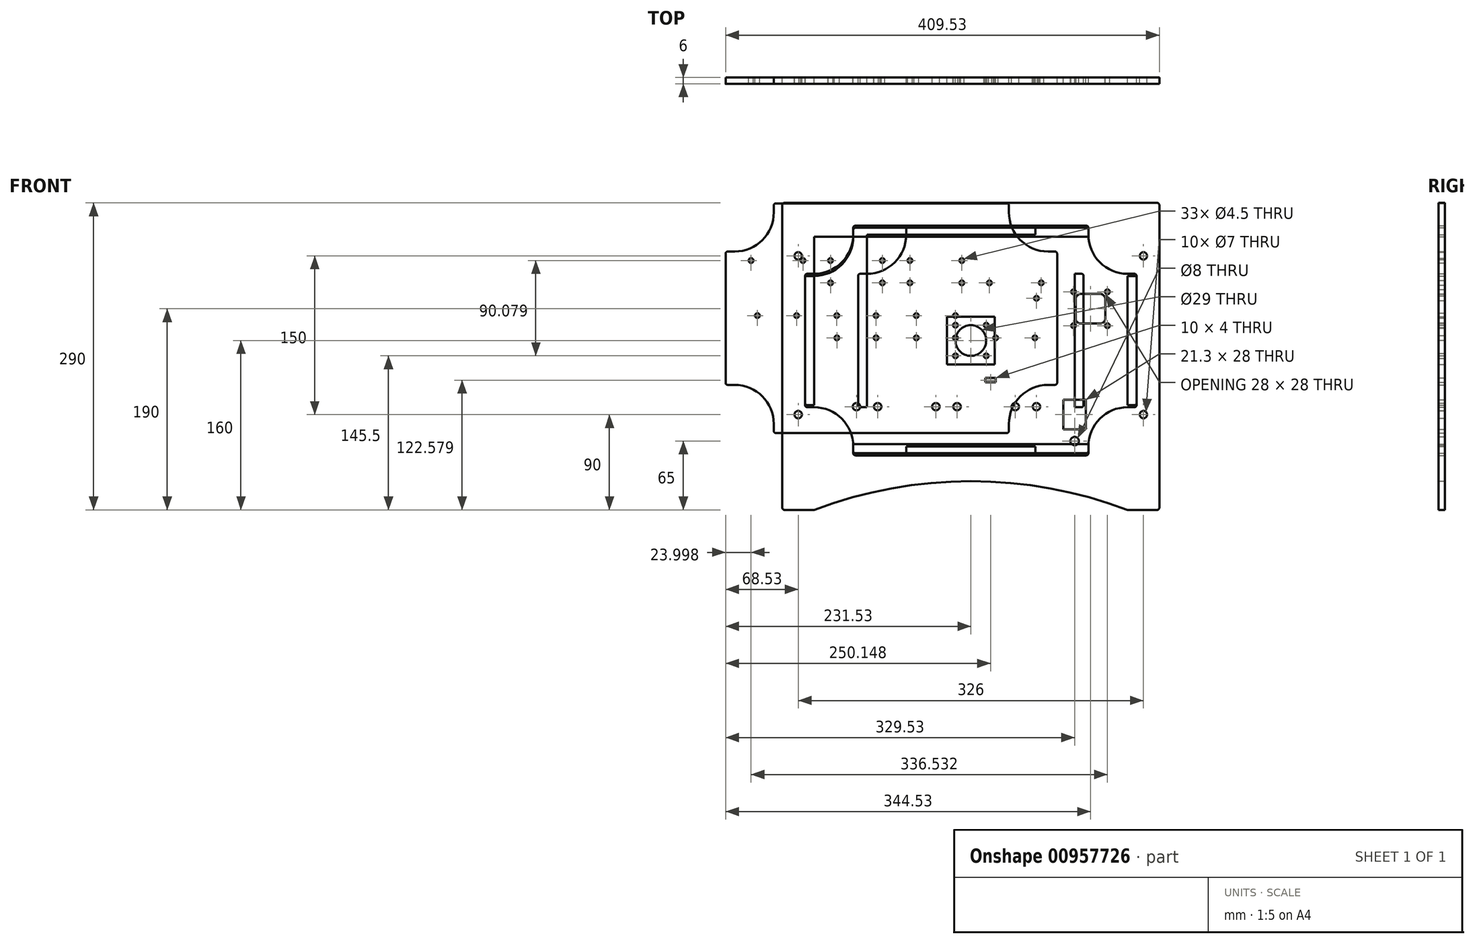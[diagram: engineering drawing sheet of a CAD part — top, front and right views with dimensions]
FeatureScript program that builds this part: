
annotation { "Feature Type Name" : "Feature", "Feature Type Description" : "" }
export const myFeature = defineFeature(function(context is Context, id is Id, definition is map)
    precondition{}
    {
        {
            var Q0;
            Q0=qCreatedBy(makeId("Front.planeOp"),FACE);
            var sketch = newSketch(context, id + "F0", { "sketchPlane" : qUnion([Q0])});
            skLineSegment(sketch, "E0.bottom", {"start": v(-148, 100) * mm, "end": v(148, 100) * mm});
            skLineSegment(sketch, "E0.top", {"start": v(-148, -100) * mm, "end": v(148, -100) * mm});
            skLineSegment(sketch, "E0.left", {"start": v(-148, 100) * mm, "end": v(-148, -100) * mm});
            skLineSegment(sketch, "E0.right", {"start": v(148, 100) * mm, "end": v(148, -100) * mm});
            skPoint(sketch, "E0.middle", {"position": v(0, 0) * mm});
            skPoint(sketch, "E1", {"position": v(-108, 30) * mm});
            skPoint(sketch, "E2", {"position": v(-33, 30) * mm});
            skPoint(sketch, "E3", {"position": v(42, 30) * mm});
            skLineSegment(sketch, "E4.bottom", {"start": v(-75.5, 62.5) * mm, "end": v(-140.5, 62.5) * mm});
            skLineSegment(sketch, "E4.top", {"start": v(-75.5, -2.5) * mm, "end": v(-140.5, -2.5) * mm});
            skLineSegment(sketch, "E4.left", {"start": v(-75.5, 62.5) * mm, "end": v(-75.5, -2.5) * mm});
            skLineSegment(sketch, "E4.right", {"start": v(-140.5, 62.5) * mm, "end": v(-140.5, -2.5) * mm});
            skLineSegment(sketch, "E5.bottom", {"start": v(-0.5, 62.5) * mm, "end": v(-65.5, 62.5) * mm});
            skLineSegment(sketch, "E5.top", {"start": v(-0.5, -2.5) * mm, "end": v(-65.5, -2.5) * mm});
            skLineSegment(sketch, "E5.left", {"start": v(-0.5, 62.5) * mm, "end": v(-0.5, -2.5) * mm});
            skLineSegment(sketch, "E5.right", {"start": v(-65.5, 62.5) * mm, "end": v(-65.5, -2.5) * mm});
            skLineSegment(sketch, "E6.bottom", {"start": v(74.5, 62.5) * mm, "end": v(9.5, 62.5) * mm});
            skLineSegment(sketch, "E6.top", {"start": v(74.5, -2.5) * mm, "end": v(9.5, -2.5) * mm});
            skLineSegment(sketch, "E6.left", {"start": v(74.5, 62.5) * mm, "end": v(74.5, -2.5) * mm});
            skLineSegment(sketch, "E6.right", {"start": v(9.5, 62.5) * mm, "end": v(9.5, -2.5) * mm});
            skPoint(sketch, "E7", {"position": v(-132.5, 54.5) * mm});
            skCircle(sketch, "E8", {"center": v(-132.5, 54.5) * mm, "radius": 2.25 * mm});
            skPoint(sketch, "E9", {"position": v(-57.5, 54.5) * mm});
            skPoint(sketch, "E10", {"position": v(17.5, 54.5) * mm});
            skCircle(sketch, "E11", {"center": v(-57.5, 54.5) * mm, "radius": 2.25 * mm});
            skCircle(sketch, "E12", {"center": v(17.5, 54.5) * mm, "radius": 2.25 * mm});
            skLineSegment(sketch, "E13", {"start": v(-33, 62.5) * mm, "end": v(-33, -2.5) * mm});
            skLineSegment(sketch, "E14", {"start": v(42, 62.5) * mm, "end": v(42, -2.5) * mm});
            skLineSegment(sketch, "E15", {"start": v(-108, 62.5) * mm, "end": v(-108, -2.5) * mm});
            skPoint(sketch, "E16", {"position": v(-126.5, 2.5) * mm});
            skPoint(sketch, "E17", {"position": v(-51.5, 2.5) * mm});
            skPoint(sketch, "E18", {"position": v(23.5, 2.5) * mm});
            skCircle(sketch, "E19", {"center": v(23.5, 2.5) * mm, "radius": 2.25 * mm});
            skCircle(sketch, "E20", {"center": v(-51.5, 2.5) * mm, "radius": 2.25 * mm});
            skCircle(sketch, "E21", {"center": v(-126.5, 2.5) * mm, "radius": 2.25 * mm});
            skArc(sketch, "E22", {"start": v(-111, 100) * mm, "mid": v(-121.84, 73.84) * mm, "end": v(-148, 63) * mm});
            skArc(sketch, "E23", {"start": v(111, 100) * mm, "mid": v(121.84, 73.84) * mm, "end": v(148, 63) * mm});
            skArc(sketch, "E24", {"start": v(148, -63) * mm, "mid": v(121.84, -73.84) * mm, "end": v(111, -100) * mm});
            skArc(sketch, "E25", {"start": v(-148, -63) * mm, "mid": v(-121.84, -73.84) * mm, "end": v(-111, -100) * mm});
            skPoint(sketch, "E26", {"position": v(-108, -62.5) * mm});
            skPoint(sketch, "E27", {"position": v(-88, -62.5) * mm});
            skPoint(sketch, "E28", {"position": v(-33, -62.5) * mm});
            skPoint(sketch, "E29", {"position": v(-13, -62.5) * mm});
            skPoint(sketch, "E30", {"position": v(42, -62.5) * mm});
            skPoint(sketch, "E31", {"position": v(62, -62.5) * mm});
            skCircle(sketch, "E32", {"center": v(-108, -62.5) * mm, "radius": 3.5 * mm});
            skCircle(sketch, "E33", {"center": v(-88, -62.5) * mm, "radius": 3.5 * mm});
            skCircle(sketch, "E34", {"center": v(-33, -62.5) * mm, "radius": 3.5 * mm});
            skCircle(sketch, "E35", {"center": v(-13, -62.5) * mm, "radius": 3.5 * mm});
            skCircle(sketch, "E36", {"center": v(42, -62.5) * mm, "radius": 3.5 * mm});
            skCircle(sketch, "E37", {"center": v(62, -62.5) * mm, "radius": 3.5 * mm});
            skPoint(sketch, "E38", {"position": v(98, -70) * mm});
            skLineSegment(sketch, "E39.bottom", {"start": v(87.35, -56) * mm, "end": v(108.65, -56) * mm});
            skLineSegment(sketch, "E39.top", {"start": v(87.35, -84) * mm, "end": v(108.65, -84) * mm});
            skLineSegment(sketch, "E39.left", {"start": v(87.35, -56) * mm, "end": v(87.35, -84) * mm});
            skLineSegment(sketch, "E39.right", {"start": v(108.65, -56) * mm, "end": v(108.65, -84) * mm});
            skPoint(sketch, "E40", {"position": v(113, 30) * mm});
            skLineSegment(sketch, "E41.bottom", {"start": v(132.75, 49.75) * mm, "end": v(93.25, 49.75) * mm});
            skLineSegment(sketch, "E41.top", {"start": v(132.75, 10.25) * mm, "end": v(93.25, 10.25) * mm});
            skLineSegment(sketch, "E41.left", {"start": v(132.75, 49.75) * mm, "end": v(132.75, 10.25) * mm});
            skLineSegment(sketch, "E41.right", {"start": v(93.25, 49.75) * mm, "end": v(93.25, 10.25) * mm});
            skPoint(sketch, "E42", {"position": v(97, 46) * mm});
            skCircle(sketch, "E43", {"center": v(97, 46) * mm, "radius": 2.25 * mm});
            skPoint(sketch, "E44.0.1.0", {"position": v(97, 14) * mm});
            skCircle(sketch, "E44.0.1.1", {"center": v(97, 14) * mm, "radius": 2.25 * mm});
            skPoint(sketch, "E44.1.0.0", {"position": v(129, 46) * mm});
            skCircle(sketch, "E44.1.0.1", {"center": v(129, 46) * mm, "radius": 2.25 * mm});
            skPoint(sketch, "E44.1.1.0", {"position": v(129, 14) * mm});
            skCircle(sketch, "E44.1.1.1", {"center": v(129, 14) * mm, "radius": 2.25 * mm});
            skLineSegment(sketch, "E44.direction1", {"start": v(97, 46) * mm, "end": v(129, 46) * mm, "construction": true});
            skLineSegment(sketch, "E44.direction2", {"start": v(97, 46) * mm, "end": v(97, 14) * mm, "construction": true});
            skCircle(sketch, "E45.MirrorC", {"center": v(-83.5, 54.5) * mm, "radius": 2.25 * mm});
            skCircle(sketch, "E46.MirrorC", {"center": v(-89.5, 2.5) * mm, "radius": 2.25 * mm});
            skCircle(sketch, "E47.MirrorC", {"center": v(-8.5, 54.5) * mm, "radius": 2.25 * mm});
            skCircle(sketch, "E48.MirrorC", {"center": v(-14.5, 2.5) * mm, "radius": 2.25 * mm});
            skCircle(sketch, "E49.MirrorC", {"center": v(66.5, 54.5) * mm, "radius": 2.25 * mm});
            skCircle(sketch, "E50.MirrorC", {"center": v(60.5, 2.5) * mm, "radius": 2.25 * mm});
            skLineSegment(sketch, "E51.bottom", {"start": v(122, 16) * mm, "end": v(104, 16) * mm});
            skLineSegment(sketch, "E51.top", {"start": v(122, 44) * mm, "end": v(104, 44) * mm});
            skLineSegment(sketch, "E51.left", {"start": v(127, 21) * mm, "end": v(127, 39) * mm});
            skLineSegment(sketch, "E51.right", {"start": v(99, 21) * mm, "end": v(99, 39) * mm});
            skPoint(sketch, "E52.visualSharp", {"position": v(99, 44) * mm});
            skArc(sketch, "E52.filletArc", {"start": v(104, 44) * mm, "mid": v(100.46, 42.54) * mm, "end": v(99, 39) * mm});
            skPoint(sketch, "E53.visualSharp", {"position": v(127, 44) * mm});
            skArc(sketch, "E53.filletArc", {"start": v(127, 39) * mm, "mid": v(125.54, 42.54) * mm, "end": v(122, 44) * mm});
            skPoint(sketch, "E54.visualSharp", {"position": v(127, 16) * mm});
            skArc(sketch, "E54.filletArc", {"start": v(122, 16) * mm, "mid": v(125.54, 17.46) * mm, "end": v(127, 21) * mm});
            skPoint(sketch, "E55.visualSharp", {"position": v(99, 16) * mm});
            skArc(sketch, "E55.filletArc", {"start": v(99, 21) * mm, "mid": v(100.46, 17.46) * mm, "end": v(104, 16) * mm});
            skLineSegment(sketch, "E56.bottom", {"start": v(-111, 100) * mm, "end": v(111, 100) * mm});
            skLineSegment(sketch, "E56.top", {"start": v(-109, 108.5) * mm, "end": v(109, 108.5) * mm});
            skLineSegment(sketch, "E56.left", {"start": v(-111, 100) * mm, "end": v(-111, 106.5) * mm});
            skLineSegment(sketch, "E56.right", {"start": v(111, 100) * mm, "end": v(111, 106.5) * mm});
            skLineSegment(sketch, "E57.bottom", {"start": v(-111, -100) * mm, "end": v(111, -100) * mm});
            skLineSegment(sketch, "E57.top", {"start": v(-109, -108.5) * mm, "end": v(109, -108.5) * mm});
            skLineSegment(sketch, "E57.left", {"start": v(-111, -100) * mm, "end": v(-111, -106.5) * mm});
            skLineSegment(sketch, "E57.right", {"start": v(111, -100) * mm, "end": v(111, -106.5) * mm});
            skLineSegment(sketch, "E58.bottom", {"start": v(-148, 63) * mm, "end": v(-154.5, 63) * mm});
            skLineSegment(sketch, "E58.top", {"start": v(-148, -63) * mm, "end": v(-154.5, -63) * mm});
            skLineSegment(sketch, "E58.left", {"start": v(-148, 63) * mm, "end": v(-148, -63) * mm});
            skLineSegment(sketch, "E58.right", {"start": v(-156.5, 61) * mm, "end": v(-156.5, -61) * mm});
            skLineSegment(sketch, "E59.bottom", {"start": v(148, 63) * mm, "end": v(154.5, 63) * mm});
            skLineSegment(sketch, "E59.top", {"start": v(148, -63) * mm, "end": v(154.5, -63) * mm});
            skLineSegment(sketch, "E59.left", {"start": v(148, 63) * mm, "end": v(148, -63) * mm});
            skLineSegment(sketch, "E59.right", {"start": v(156.5, 61) * mm, "end": v(156.5, -61) * mm});
            skPoint(sketch, "E60.visualSharp", {"position": v(-111, 108.5) * mm});
            skArc(sketch, "E60.filletArc", {"start": v(-109, 108.5) * mm, "mid": v(-110.41, 107.91) * mm, "end": v(-111, 106.5) * mm});
            skPoint(sketch, "E61.visualSharp", {"position": v(111, 108.5) * mm});
            skArc(sketch, "E61.filletArc", {"start": v(111, 106.5) * mm, "mid": v(110.41, 107.91) * mm, "end": v(109, 108.5) * mm});
            skPoint(sketch, "E62.visualSharp", {"position": v(156.5, 63) * mm});
            skArc(sketch, "E62.filletArc", {"start": v(156.5, 61) * mm, "mid": v(155.91, 62.41) * mm, "end": v(154.5, 63) * mm});
            skPoint(sketch, "E63.visualSharp", {"position": v(156.5, -63) * mm});
            skArc(sketch, "E63.filletArc", {"start": v(154.5, -63) * mm, "mid": v(155.91, -62.41) * mm, "end": v(156.5, -61) * mm});
            skPoint(sketch, "E64.visualSharp", {"position": v(111, -108.5) * mm});
            skArc(sketch, "E64.filletArc", {"start": v(109, -108.5) * mm, "mid": v(110.41, -107.91) * mm, "end": v(111, -106.5) * mm});
            skPoint(sketch, "E65.visualSharp", {"position": v(-111, -108.5) * mm});
            skArc(sketch, "E65.filletArc", {"start": v(-111, -106.5) * mm, "mid": v(-110.41, -107.91) * mm, "end": v(-109, -108.5) * mm});
            skPoint(sketch, "E66.visualSharp", {"position": v(-156.5, -63) * mm});
            skArc(sketch, "E66.filletArc", {"start": v(-156.5, -61) * mm, "mid": v(-155.91, -62.41) * mm, "end": v(-154.5, -63) * mm});
            skPoint(sketch, "E67.visualSharp", {"position": v(-156.5, 63) * mm});
            skArc(sketch, "E67.filletArc", {"start": v(-154.5, 63) * mm, "mid": v(-155.91, 62.41) * mm, "end": v(-156.5, 61) * mm});
            skPoint(sketch, "E68", {"position": v(98, -95) * mm});
            skPoint(sketch, "E68.positionSnap0", {"position": v(98, -84) * mm});
            skCircle(sketch, "E69", {"center": v(98, -95) * mm, "radius": 4 * mm});
            skSolve(sketch);
        }
        {
            var Q0;
            {var subQ28=sQuery(id+"F0.wireOp",EDGE,"E4.left");Q0=makeQuery(id+"F0.imprint","IMPRINT",FACE,{"disambiguationData":[TD([[makeQuery(id+"F0.imprint","IMPRINT",EDGE,{"derivedFrom":subQ28}),1.0]])]});}
            var Q1;
            {var subQ0=sQuery(id+"F0.wireOp",EDGE,"E4.left");Q1=makeQuery(id+"F0.imprint","IMPRINT",FACE,{"disambiguationData":[TD([[makeQuery(id+"F0.imprint","IMPRINT",EDGE,{"derivedFrom":subQ0}),-1.0]])]});}
            var Q2;
            {var subQ0=sQuery(id+"F0.wireOp",EDGE,"E5.right");Q2=makeQuery(id+"F0.imprint","IMPRINT",FACE,{"disambiguationData":[TD([[makeQuery(id+"F0.imprint","IMPRINT",EDGE,{"derivedFrom":subQ0}),1.0]])]});}
            var Q3;
            {var subQ1=sQuery(id+"F0.wireOp",EDGE,"E5.left");Q3=makeQuery(id+"F0.imprint","IMPRINT",FACE,{"disambiguationData":[TD([[makeQuery(id+"F0.imprint","IMPRINT",EDGE,{"derivedFrom":subQ1}),-1.0]])]});}
            var Q4;
            {var subQ2=sQuery(id+"F0.wireOp",EDGE,"E4.right");Q4=makeQuery(id+"F0.imprint","IMPRINT",FACE,{"disambiguationData":[TD([[makeQuery(id+"F0.imprint","IMPRINT",EDGE,{"derivedFrom":subQ2}),1.0]])]});}
            var Q5;
            {var subQ0=sQuery(id+"F0.wireOp",EDGE,"E6.right");Q5=makeQuery(id+"F0.imprint","IMPRINT",FACE,{"disambiguationData":[TD([[makeQuery(id+"F0.imprint","IMPRINT",EDGE,{"derivedFrom":subQ0}),1.0]])]});}
            var Q6;
            {var subQ0=sQuery(id+"F0.wireOp",EDGE,"E6.left");Q6=makeQuery(id+"F0.imprint","IMPRINT",FACE,{"disambiguationData":[TD([[makeQuery(id+"F0.imprint","IMPRINT",EDGE,{"derivedFrom":subQ0}),-1.0]])]});}
            var Q7;
            Q7=makeQuery(id+"F0.imprint","IMPRINT",FACE,{"disambiguationData":[TD([[makeQuery(id+"F0.imprint","IMPRINT",EDGE,{"derivedFrom":sQuery(id+"F0.wireOp",EDGE,"E41.bottom")}),1.0]])]});
            var Q8;
            {var subQ0=sQuery(id+"F0.wireOp",EDGE,"E58.bottom");Q8=makeQuery(id+"F0.imprint","IMPRINT",FACE,{"disambiguationData":[TD([[makeQuery(id+"F0.imprint","IMPRINT",EDGE,{"derivedFrom":subQ0}),1.0]])]});}
            var Q9;
            Q9=makeQuery(id+"F0.imprint","IMPRINT",FACE,{"disambiguationData":[TD([[makeQuery(id+"F0.imprint","IMPRINT",EDGE,{"derivedFrom":sQuery(id+"F0.wireOp",EDGE,"E56.top")}),-1.0]])]});
            var Q10;
            {var subQ0=sQuery(id+"F0.wireOp",EDGE,"E59.bottom");Q10=makeQuery(id+"F0.imprint","IMPRINT",FACE,{"disambiguationData":[TD([[makeQuery(id+"F0.imprint","IMPRINT",EDGE,{"derivedFrom":subQ0}),-1.0]])]});}
            var Q11;
            Q11=makeQuery(id+"F0.imprint","IMPRINT",FACE,{"disambiguationData":[TD([[makeQuery(id+"F0.imprint","IMPRINT",EDGE,{"derivedFrom":sQuery(id+"F0.wireOp",EDGE,"E57.top")}),1.0]])]});
            extrude(context, id + "F1", {"entities" : qUnion([Q0, Q1, Q2, Q3, Q4, Q5, Q6, Q7, Q8, Q9, Q10, Q11]), "depth" : 6 * mm, "offsetDistance" : 25 * mm});
        }
        {
            var Q0;
            Q0=qCreatedBy(makeId("Front.planeOp"),FACE);
            var sketch = newSketch(context, id + "F2", { "sketchPlane" : qUnion([Q0])});
            skLineSegment(sketch, "E70.bottom", {"start": v(-223.03, 121.08) * mm, "end": v(72.97, 121.08) * mm});
            skLineSegment(sketch, "E70.top", {"start": v(-223.03, -78.92) * mm, "end": v(72.97, -78.92) * mm});
            skLineSegment(sketch, "E70.left", {"start": v(-223.03, 121.08) * mm, "end": v(-223.03, -78.92) * mm});
            skLineSegment(sketch, "E70.right", {"start": v(72.97, 121.08) * mm, "end": v(72.97, -78.92) * mm});
            skPoint(sketch, "E70.middle", {"position": v(-75.03, 21.08) * mm});
            skPoint(sketch, "E71", {"position": v(-183.03, 51.08) * mm});
            skPoint(sketch, "E72", {"position": v(-108.03, 51.08) * mm});
            skPoint(sketch, "E73", {"position": v(-33.03, 51.08) * mm});
            skLineSegment(sketch, "E74.bottom", {"start": v(-150.53, 83.58) * mm, "end": v(-215.53, 83.58) * mm});
            skLineSegment(sketch, "E74.top", {"start": v(-150.53, 18.58) * mm, "end": v(-215.53, 18.58) * mm});
            skLineSegment(sketch, "E74.left", {"start": v(-150.53, 83.58) * mm, "end": v(-150.53, 18.58) * mm});
            skLineSegment(sketch, "E74.right", {"start": v(-215.53, 83.58) * mm, "end": v(-215.53, 18.58) * mm});
            skLineSegment(sketch, "E75.bottom", {"start": v(-75.53, 83.58) * mm, "end": v(-140.53, 83.58) * mm});
            skLineSegment(sketch, "E75.top", {"start": v(-75.53, 18.58) * mm, "end": v(-140.53, 18.58) * mm});
            skLineSegment(sketch, "E75.left", {"start": v(-75.53, 83.58) * mm, "end": v(-75.53, 18.58) * mm});
            skLineSegment(sketch, "E75.right", {"start": v(-140.53, 83.58) * mm, "end": v(-140.53, 18.58) * mm});
            skLineSegment(sketch, "E76.bottom", {"start": v(-0.53, 83.58) * mm, "end": v(-65.53, 83.58) * mm});
            skLineSegment(sketch, "E76.top", {"start": v(-0.53, 18.58) * mm, "end": v(-65.53, 18.58) * mm});
            skLineSegment(sketch, "E76.left", {"start": v(-0.53, 83.58) * mm, "end": v(-0.53, 18.58) * mm});
            skLineSegment(sketch, "E76.right", {"start": v(-65.53, 83.58) * mm, "end": v(-65.53, 18.58) * mm});
            skPoint(sketch, "E77", {"position": v(-207.53, 75.58) * mm});
            skCircle(sketch, "E78", {"center": v(-207.53, 75.58) * mm, "radius": 2.25 * mm});
            skPoint(sketch, "E79", {"position": v(-132.53, 75.58) * mm});
            skPoint(sketch, "E80", {"position": v(-57.53, 75.58) * mm});
            skCircle(sketch, "E81", {"center": v(-132.53, 75.58) * mm, "radius": 2.25 * mm});
            skCircle(sketch, "E82", {"center": v(-57.53, 75.58) * mm, "radius": 2.25 * mm});
            skLineSegment(sketch, "E83", {"start": v(-108.03, 83.58) * mm, "end": v(-108.03, 18.58) * mm});
            skLineSegment(sketch, "E84", {"start": v(-33.03, 83.58) * mm, "end": v(-33.03, 18.58) * mm});
            skLineSegment(sketch, "E85", {"start": v(-183.03, 83.58) * mm, "end": v(-183.03, 18.58) * mm});
            skPoint(sketch, "E86", {"position": v(-201.53, 23.58) * mm});
            skPoint(sketch, "E87", {"position": v(-126.53, 23.58) * mm});
            skPoint(sketch, "E88", {"position": v(-51.53, 23.58) * mm});
            skCircle(sketch, "E89", {"center": v(-51.53, 23.58) * mm, "radius": 2.25 * mm});
            skCircle(sketch, "E90", {"center": v(-126.53, 23.58) * mm, "radius": 2.25 * mm});
            skCircle(sketch, "E91", {"center": v(-201.53, 23.58) * mm, "radius": 2.25 * mm});
            skArc(sketch, "E92", {"start": v(-186.03, 121.08) * mm, "mid": v(-196.87, 94.92) * mm, "end": v(-223.03, 84.08) * mm});
            skArc(sketch, "E93", {"start": v(35.97, 121.08) * mm, "mid": v(46.8, 94.92) * mm, "end": v(72.97, 84.08) * mm});
            skArc(sketch, "E94", {"start": v(72.97, -41.92) * mm, "mid": v(46.8, -52.76) * mm, "end": v(35.97, -78.92) * mm});
            skArc(sketch, "E95", {"start": v(-223.03, -41.92) * mm, "mid": v(-196.87, -52.76) * mm, "end": v(-186.03, -78.92) * mm});
            skCircle(sketch, "E96.MirrorC", {"center": v(-158.53, 75.58) * mm, "radius": 2.25 * mm});
            skCircle(sketch, "E97.MirrorC", {"center": v(-164.53, 23.58) * mm, "radius": 2.25 * mm});
            skCircle(sketch, "E98.MirrorC", {"center": v(-83.53, 75.58) * mm, "radius": 2.25 * mm});
            skCircle(sketch, "E99.MirrorC", {"center": v(-89.53, 23.58) * mm, "radius": 2.25 * mm});
            skCircle(sketch, "E100.MirrorC", {"center": v(-8.53, 75.58) * mm, "radius": 2.25 * mm});
            skCircle(sketch, "E101.MirrorC", {"center": v(-14.53, 23.58) * mm, "radius": 2.25 * mm});
            skLineSegment(sketch, "E102.bottom", {"start": v(-186.03, 121.08) * mm, "end": v(35.97, 121.08) * mm});
            skLineSegment(sketch, "E102.top", {"start": v(-184.03, 129.58) * mm, "end": v(33.97, 129.58) * mm});
            skLineSegment(sketch, "E102.left", {"start": v(-186.03, 121.08) * mm, "end": v(-186.03, 127.58) * mm});
            skLineSegment(sketch, "E102.right", {"start": v(35.97, 121.08) * mm, "end": v(35.97, 127.58) * mm});
            skLineSegment(sketch, "E103.bottom", {"start": v(-186.03, -78.92) * mm, "end": v(35.97, -78.92) * mm});
            skLineSegment(sketch, "E103.top", {"start": v(-184.03, -87.42) * mm, "end": v(33.97, -87.42) * mm});
            skLineSegment(sketch, "E103.left", {"start": v(-186.03, -78.92) * mm, "end": v(-186.03, -85.42) * mm});
            skLineSegment(sketch, "E103.right", {"start": v(35.97, -78.92) * mm, "end": v(35.97, -85.42) * mm});
            skLineSegment(sketch, "E104.bottom", {"start": v(-223.03, 84.08) * mm, "end": v(-229.53, 84.08) * mm});
            skLineSegment(sketch, "E104.top", {"start": v(-223.03, -41.92) * mm, "end": v(-229.53, -41.92) * mm});
            skLineSegment(sketch, "E104.left", {"start": v(-223.03, 84.08) * mm, "end": v(-223.03, -41.92) * mm});
            skLineSegment(sketch, "E104.right", {"start": v(-231.53, 82.08) * mm, "end": v(-231.53, -39.92) * mm});
            skLineSegment(sketch, "E105.bottom", {"start": v(72.97, 84.08) * mm, "end": v(79.47, 84.08) * mm});
            skLineSegment(sketch, "E105.top", {"start": v(72.97, -41.92) * mm, "end": v(79.47, -41.92) * mm});
            skLineSegment(sketch, "E105.left", {"start": v(72.97, 84.08) * mm, "end": v(72.97, -41.92) * mm});
            skLineSegment(sketch, "E105.right", {"start": v(81.47, 82.08) * mm, "end": v(81.47, -39.92) * mm});
            skPoint(sketch, "E106", {"position": v(37.97, 1.08) * mm});
            skLineSegment(sketch, "E107.bottom", {"start": v(66.97, 43.58) * mm, "end": v(8.97, 43.58) * mm});
            skLineSegment(sketch, "E107.top", {"start": v(66.97, -41.42) * mm, "end": v(8.97, -41.42) * mm});
            skLineSegment(sketch, "E107.left", {"start": v(66.97, 43.58) * mm, "end": v(66.97, -41.42) * mm});
            skLineSegment(sketch, "E107.right", {"start": v(8.97, 43.58) * mm, "end": v(8.97, -41.42) * mm});
            skPoint(sketch, "E108", {"position": v(62.02, 39.93) * mm});
            skCircle(sketch, "E109", {"center": v(62.02, 39.93) * mm, "radius": 2.25 * mm});
            skPoint(sketch, "E110", {"position": v(13.62, -41.42) * mm});
            skLineSegment(sketch, "E111", {"start": v(13.62, -41.42) * mm, "end": v(13.62, -39.42) * mm});
            skLineSegment(sketch, "E112.bottom", {"start": v(13.62, -39.42) * mm, "end": v(23.62, -39.42) * mm});
            skLineSegment(sketch, "E112.top", {"start": v(13.62, -35.42) * mm, "end": v(23.62, -35.42) * mm});
            skLineSegment(sketch, "E112.left", {"start": v(13.62, -39.42) * mm, "end": v(13.62, -35.42) * mm});
            skLineSegment(sketch, "E112.right", {"start": v(23.62, -39.42) * mm, "end": v(23.62, -35.42) * mm});
            skPoint(sketch, "E113.visualSharp", {"position": v(-186.03, 129.58) * mm});
            skArc(sketch, "E113.filletArc", {"start": v(-184.03, 129.58) * mm, "mid": v(-185.45, 129) * mm, "end": v(-186.03, 127.58) * mm});
            skPoint(sketch, "E114.visualSharp", {"position": v(35.97, 129.58) * mm});
            skArc(sketch, "E114.filletArc", {"start": v(35.97, 127.58) * mm, "mid": v(35.38, 129) * mm, "end": v(33.97, 129.58) * mm});
            skPoint(sketch, "E115.visualSharp", {"position": v(81.47, 84.08) * mm});
            skArc(sketch, "E115.filletArc", {"start": v(81.47, 82.08) * mm, "mid": v(80.88, 83.5) * mm, "end": v(79.47, 84.08) * mm});
            skPoint(sketch, "E116.visualSharp", {"position": v(81.47, -41.92) * mm});
            skArc(sketch, "E116.filletArc", {"start": v(79.47, -41.92) * mm, "mid": v(80.88, -41.34) * mm, "end": v(81.47, -39.92) * mm});
            skPoint(sketch, "E117.visualSharp", {"position": v(35.97, -87.42) * mm});
            skArc(sketch, "E117.filletArc", {"start": v(33.97, -87.42) * mm, "mid": v(35.38, -86.84) * mm, "end": v(35.97, -85.42) * mm});
            skPoint(sketch, "E118.visualSharp", {"position": v(-186.03, -87.42) * mm});
            skArc(sketch, "E118.filletArc", {"start": v(-186.03, -85.42) * mm, "mid": v(-185.45, -86.84) * mm, "end": v(-184.03, -87.42) * mm});
            skPoint(sketch, "E119.visualSharp", {"position": v(-231.53, -41.92) * mm});
            skArc(sketch, "E119.filletArc", {"start": v(-231.53, -39.92) * mm, "mid": v(-230.95, -41.34) * mm, "end": v(-229.53, -41.92) * mm});
            skPoint(sketch, "E120.visualSharp", {"position": v(-231.53, 84.08) * mm});
            skArc(sketch, "E120.filletArc", {"start": v(-229.53, 84.08) * mm, "mid": v(-230.95, 83.5) * mm, "end": v(-231.53, 82.08) * mm});
            skSolve(sketch);
        }
        {
            var Q0;
            {var subQ24=sQuery(id+"F2.wireOp",EDGE,"E74.left");Q0=makeQuery(id+"F2.imprint","IMPRINT",FACE,{"disambiguationData":[TD([[makeQuery(id+"F2.imprint","IMPRINT",EDGE,{"derivedFrom":subQ24}),1.0]])]});}
            var Q1;
            Q1=makeQuery(id+"F2.imprint","IMPRINT",FACE,{"disambiguationData":[TD([[makeQuery(id+"F2.imprint","IMPRINT",EDGE,{"derivedFrom":sQuery(id+"F2.wireOp",EDGE,"E102.top")}),-1.0]])]});
            var Q2;
            {var subQ0=sQuery(id+"F2.wireOp",EDGE,"E105.bottom");Q2=makeQuery(id+"F2.imprint","IMPRINT",FACE,{"disambiguationData":[TD([[makeQuery(id+"F2.imprint","IMPRINT",EDGE,{"derivedFrom":subQ0}),-1.0]])]});}
            var Q3;
            {var subQ0=sQuery(id+"F2.wireOp",EDGE,"E104.bottom");Q3=makeQuery(id+"F2.imprint","IMPRINT",FACE,{"disambiguationData":[TD([[makeQuery(id+"F2.imprint","IMPRINT",EDGE,{"derivedFrom":subQ0}),1.0]])]});}
            var Q4;
            Q4=makeQuery(id+"F2.imprint","IMPRINT",FACE,{"disambiguationData":[TD([[makeQuery(id+"F2.imprint","IMPRINT",EDGE,{"derivedFrom":sQuery(id+"F2.wireOp",EDGE,"E103.top")}),1.0]])]});
            var Q5;
            Q5=makeQuery(id+"F2.imprint","IMPRINT",FACE,{"disambiguationData":[TD([[makeQuery(id+"F2.imprint","IMPRINT",EDGE,{"derivedFrom":sQuery(id+"F2.wireOp",EDGE,"E107.bottom")}),1.0]])]});
            var Q6;
            {var subQ0=sQuery(id+"F2.wireOp",EDGE,"E76.left");Q6=makeQuery(id+"F2.imprint","IMPRINT",FACE,{"disambiguationData":[TD([[makeQuery(id+"F2.imprint","IMPRINT",EDGE,{"derivedFrom":subQ0}),-1.0]])]});}
            var Q7;
            {var subQ0=sQuery(id+"F2.wireOp",EDGE,"E76.right");Q7=makeQuery(id+"F2.imprint","IMPRINT",FACE,{"disambiguationData":[TD([[makeQuery(id+"F2.imprint","IMPRINT",EDGE,{"derivedFrom":subQ0}),1.0]])]});}
            var Q8;
            {var subQ1=sQuery(id+"F2.wireOp",EDGE,"E75.left");Q8=makeQuery(id+"F2.imprint","IMPRINT",FACE,{"disambiguationData":[TD([[makeQuery(id+"F2.imprint","IMPRINT",EDGE,{"derivedFrom":subQ1}),-1.0]])]});}
            var Q9;
            {var subQ0=sQuery(id+"F2.wireOp",EDGE,"E75.right");Q9=makeQuery(id+"F2.imprint","IMPRINT",FACE,{"disambiguationData":[TD([[makeQuery(id+"F2.imprint","IMPRINT",EDGE,{"derivedFrom":subQ0}),1.0]])]});}
            var Q10;
            {var subQ2=sQuery(id+"F2.wireOp",EDGE,"E74.left");Q10=makeQuery(id+"F2.imprint","IMPRINT",FACE,{"disambiguationData":[TD([[makeQuery(id+"F2.imprint","IMPRINT",EDGE,{"derivedFrom":subQ2}),-1.0]])]});}
            var Q11;
            {var subQ0=sQuery(id+"F2.wireOp",EDGE,"E74.right");Q11=makeQuery(id+"F2.imprint","IMPRINT",FACE,{"disambiguationData":[TD([[makeQuery(id+"F2.imprint","IMPRINT",EDGE,{"derivedFrom":subQ0}),1.0]])]});}
            extrude(context, id + "F3", {"entities" : qUnion([Q0, Q1, Q2, Q3, Q4, Q5, Q6, Q7, Q8, Q9, Q10, Q11]), "depth" : 6 * mm, "offsetDistance" : 25 * mm});
        }
        {
            var Q0;
            Q0=qCreatedBy(makeId("Front.planeOp"),FACE);
            var sketch = newSketch(context, id + "F4", { "sketchPlane" : qUnion([Q0])});
            skLineSegment(sketch, "E121.bottom", {"start": v(-98, 100) * mm, "end": v(98, 100) * mm});
            skLineSegment(sketch, "E121.top", {"start": v(-98, -100) * mm, "end": v(98, -100) * mm});
            skLineSegment(sketch, "E121.left", {"start": v(-98, 100) * mm, "end": v(-98, -100) * mm});
            skLineSegment(sketch, "E121.right", {"start": v(98, 100) * mm, "end": v(98, -100) * mm});
            skPoint(sketch, "E121.middle", {"position": v(0, 0) * mm});
            skArc(sketch, "E122", {"start": v(-61, 100) * mm, "mid": v(-71.84, 73.84) * mm, "end": v(-98, 63) * mm});
            skArc(sketch, "E123", {"start": v(61, 100) * mm, "mid": v(71.84, 73.84) * mm, "end": v(98, 63) * mm});
            skArc(sketch, "E124", {"start": v(98, -63) * mm, "mid": v(71.84, -73.84) * mm, "end": v(61, -100) * mm});
            skArc(sketch, "E125", {"start": v(-98, -63) * mm, "mid": v(-71.84, -73.84) * mm, "end": v(-61, -100) * mm});
            skLineSegment(sketch, "E126.bottom", {"start": v(-61, 100) * mm, "end": v(61, 100) * mm});
            skLineSegment(sketch, "E126.top", {"start": v(-59, 108.5) * mm, "end": v(59, 108.5) * mm});
            skLineSegment(sketch, "E126.left", {"start": v(-61, 100) * mm, "end": v(-61, 106.5) * mm});
            skLineSegment(sketch, "E126.right", {"start": v(61, 100) * mm, "end": v(61, 106.5) * mm});
            skLineSegment(sketch, "E127.bottom", {"start": v(-61, -100) * mm, "end": v(61, -100) * mm});
            skLineSegment(sketch, "E127.top", {"start": v(-59, -108.5) * mm, "end": v(59, -108.5) * mm});
            skLineSegment(sketch, "E127.left", {"start": v(-61, -100) * mm, "end": v(-61, -106.5) * mm});
            skLineSegment(sketch, "E127.right", {"start": v(61, -100) * mm, "end": v(61, -106.5) * mm});
            skLineSegment(sketch, "E128.bottom", {"start": v(-98, -63) * mm, "end": v(-104.5, -63) * mm});
            skLineSegment(sketch, "E128.top", {"start": v(-98, 63) * mm, "end": v(-104.5, 63) * mm});
            skLineSegment(sketch, "E128.left", {"start": v(-98, -63) * mm, "end": v(-98, 63) * mm});
            skLineSegment(sketch, "E128.right", {"start": v(-106.5, -61) * mm, "end": v(-106.5, 61) * mm});
            skLineSegment(sketch, "E129.bottom", {"start": v(98, 63) * mm, "end": v(104.5, 63) * mm});
            skLineSegment(sketch, "E129.top", {"start": v(98, -63) * mm, "end": v(104.5, -63) * mm});
            skLineSegment(sketch, "E129.left", {"start": v(98, 63) * mm, "end": v(98, -63) * mm});
            skLineSegment(sketch, "E129.right", {"start": v(106.5, 61) * mm, "end": v(106.5, -61) * mm});
            skPoint(sketch, "E130.visualSharp", {"position": v(-61, 108.5) * mm});
            skArc(sketch, "E130.filletArc", {"start": v(-59, 108.5) * mm, "mid": v(-60.41, 107.91) * mm, "end": v(-61, 106.5) * mm});
            skPoint(sketch, "E131.visualSharp", {"position": v(61, 108.5) * mm});
            skArc(sketch, "E131.filletArc", {"start": v(61, 106.5) * mm, "mid": v(60.41, 107.91) * mm, "end": v(59, 108.5) * mm});
            skPoint(sketch, "E132.visualSharp", {"position": v(106.5, 63) * mm});
            skArc(sketch, "E132.filletArc", {"start": v(106.5, 61) * mm, "mid": v(105.91, 62.41) * mm, "end": v(104.5, 63) * mm});
            skPoint(sketch, "E133.visualSharp", {"position": v(-106.5, 63) * mm});
            skArc(sketch, "E133.filletArc", {"start": v(-104.5, 63) * mm, "mid": v(-105.91, 62.41) * mm, "end": v(-106.5, 61) * mm});
            skPoint(sketch, "E134.visualSharp", {"position": v(106.5, -63) * mm});
            skArc(sketch, "E134.filletArc", {"start": v(104.5, -63) * mm, "mid": v(105.91, -62.41) * mm, "end": v(106.5, -61) * mm});
            skPoint(sketch, "E135.visualSharp", {"position": v(61, -108.5) * mm});
            skArc(sketch, "E135.filletArc", {"start": v(59, -108.5) * mm, "mid": v(60.41, -107.91) * mm, "end": v(61, -106.5) * mm});
            skPoint(sketch, "E136.visualSharp", {"position": v(-61, -108.5) * mm});
            skArc(sketch, "E136.filletArc", {"start": v(-61, -106.5) * mm, "mid": v(-60.41, -107.91) * mm, "end": v(-59, -108.5) * mm});
            skPoint(sketch, "E137.visualSharp", {"position": v(-106.5, -63) * mm});
            skArc(sketch, "E137.filletArc", {"start": v(-106.5, -61) * mm, "mid": v(-105.91, -62.41) * mm, "end": v(-104.5, -63) * mm});
            skSolve(sketch);
        }
        {
            var Q0;
            {var subQ3=sQuery(id+"F4.wireOp",EDGE,"E122");Q0=makeQuery(id+"F4.imprint","IMPRINT",FACE,{"disambiguationData":[TD([[makeQuery(id+"F4.imprint","IMPRINT",EDGE,{"derivedFrom":subQ3}),1.0]])]});}
            var Q1;
            {var subQ1=sQuery(id+"F4.wireOp",EDGE,"E128.bottom");Q1=makeQuery(id+"F4.imprint","IMPRINT",FACE,{"disambiguationData":[TD([[makeQuery(id+"F4.imprint","IMPRINT",EDGE,{"derivedFrom":subQ1}),-1.0]])]});}
            var Q2;
            Q2=makeQuery(id+"F4.imprint","IMPRINT",FACE,{"disambiguationData":[TD([[makeQuery(id+"F4.imprint","IMPRINT",EDGE,{"derivedFrom":sQuery(id+"F4.wireOp",EDGE,"E126.top")}),-1.0]])]});
            var Q3;
            {var subQ1=sQuery(id+"F4.wireOp",EDGE,"E129.bottom");Q3=makeQuery(id+"F4.imprint","IMPRINT",FACE,{"disambiguationData":[TD([[makeQuery(id+"F4.imprint","IMPRINT",EDGE,{"derivedFrom":subQ1}),-1.0]])]});}
            var Q4;
            Q4=makeQuery(id+"F4.imprint","IMPRINT",FACE,{"disambiguationData":[TD([[makeQuery(id+"F4.imprint","IMPRINT",EDGE,{"derivedFrom":sQuery(id+"F4.wireOp",EDGE,"E127.top")}),1.0]])]});
            extrude(context, id + "F5", {"entities" : qUnion([Q0, Q1, Q2, Q3, Q4]), "depth" : 6 * mm, "offsetDistance" : 25 * mm});
        }
        {
            var Q0;
            Q0=qCreatedBy(makeId("Front.planeOp"),FACE);
            var sketch = newSketch(context, id + "F6", { "sketchPlane" : qUnion([Q0])});
            skLineSegment(sketch, "E138.bottom", {"start": v(98, 100) * mm, "end": v(-98, 100) * mm});
            skLineSegment(sketch, "E138.top", {"start": v(98, -100) * mm, "end": v(-98, -100) * mm});
            skLineSegment(sketch, "E138.left", {"start": v(98, 100) * mm, "end": v(98, -100) * mm});
            skLineSegment(sketch, "E138.right", {"start": v(-98, 100) * mm, "end": v(-98, -100) * mm});
            skPoint(sketch, "E138.middle", {"position": v(0, 0) * mm});
            skArc(sketch, "E139", {"start": v(-61, 100) * mm, "mid": v(-71.84, 73.84) * mm, "end": v(-98, 63) * mm});
            skArc(sketch, "E140", {"start": v(61, 100) * mm, "mid": v(71.84, 73.84) * mm, "end": v(98, 63) * mm});
            skArc(sketch, "E141", {"start": v(98, -63) * mm, "mid": v(71.84, -73.84) * mm, "end": v(61, -100) * mm});
            skArc(sketch, "E142", {"start": v(-98, -63) * mm, "mid": v(-71.84, -73.84) * mm, "end": v(-61, -100) * mm});
            skLineSegment(sketch, "E143.bottom", {"start": v(-61, 100) * mm, "end": v(61, 100) * mm});
            skLineSegment(sketch, "E143.top", {"start": v(-59, 108.5) * mm, "end": v(59, 108.5) * mm});
            skLineSegment(sketch, "E143.left", {"start": v(-61, 100) * mm, "end": v(-61, 106.5) * mm});
            skLineSegment(sketch, "E143.right", {"start": v(61, 100) * mm, "end": v(61, 106.5) * mm});
            skLineSegment(sketch, "E144.bottom", {"start": v(61, -100) * mm, "end": v(-61, -100) * mm});
            skLineSegment(sketch, "E144.top", {"start": v(59, -108.5) * mm, "end": v(-59, -108.5) * mm});
            skLineSegment(sketch, "E144.left", {"start": v(61, -100) * mm, "end": v(61, -106.5) * mm});
            skLineSegment(sketch, "E144.right", {"start": v(-61, -100) * mm, "end": v(-61, -106.5) * mm});
            skLineSegment(sketch, "E145.bottom", {"start": v(-98, -63) * mm, "end": v(-104.5, -63) * mm});
            skLineSegment(sketch, "E145.top", {"start": v(-98, 63) * mm, "end": v(-104.5, 63) * mm});
            skLineSegment(sketch, "E145.left", {"start": v(-98, -63) * mm, "end": v(-98, 63) * mm});
            skLineSegment(sketch, "E145.right", {"start": v(-106.5, -61) * mm, "end": v(-106.5, 61) * mm});
            skPoint(sketch, "E146", {"position": v(-68, 70) * mm});
            skCircle(sketch, "E147", {"center": v(-68, 70) * mm, "radius": 2.25 * mm});
            skCircle(sketch, "E148.0.1.0", {"center": v(-68, -70) * mm, "radius": 2.25 * mm});
            skPoint(sketch, "E148.0.1.1", {"position": v(-68, -70) * mm});
            skCircle(sketch, "E148.1.0.0", {"center": v(68, 70) * mm, "radius": 2.25 * mm});
            skPoint(sketch, "E148.1.0.1", {"position": v(68, 70) * mm});
            skCircle(sketch, "E148.1.1.0", {"center": v(68, -70) * mm, "radius": 2.25 * mm});
            skPoint(sketch, "E148.1.1.1", {"position": v(68, -70) * mm});
            skLineSegment(sketch, "E148.direction1", {"start": v(-68, 70) * mm, "end": v(68, 70) * mm, "construction": true});
            skLineSegment(sketch, "E148.direction2", {"start": v(-68, 70) * mm, "end": v(-68, -70) * mm, "construction": true});
            skLineSegment(sketch, "E149.bottom", {"start": v(98, 63) * mm, "end": v(104.5, 63) * mm});
            skLineSegment(sketch, "E149.top", {"start": v(98, -63) * mm, "end": v(104.5, -63) * mm});
            skLineSegment(sketch, "E149.left", {"start": v(98, 63) * mm, "end": v(98, -63) * mm});
            skLineSegment(sketch, "E149.right", {"start": v(106.5, 61) * mm, "end": v(106.5, -61) * mm});
            skPoint(sketch, "E150.visualSharp", {"position": v(-61, 108.5) * mm});
            skArc(sketch, "E150.filletArc", {"start": v(-59, 108.5) * mm, "mid": v(-60.41, 107.91) * mm, "end": v(-61, 106.5) * mm});
            skPoint(sketch, "E151.visualSharp", {"position": v(61, 108.5) * mm});
            skArc(sketch, "E151.filletArc", {"start": v(61, 106.5) * mm, "mid": v(60.41, 107.91) * mm, "end": v(59, 108.5) * mm});
            skPoint(sketch, "E152.visualSharp", {"position": v(106.5, 63) * mm});
            skArc(sketch, "E152.filletArc", {"start": v(106.5, 61) * mm, "mid": v(105.91, 62.41) * mm, "end": v(104.5, 63) * mm});
            skPoint(sketch, "E153.visualSharp", {"position": v(106.5, -63) * mm});
            skArc(sketch, "E153.filletArc", {"start": v(104.5, -63) * mm, "mid": v(105.91, -62.41) * mm, "end": v(106.5, -61) * mm});
            skPoint(sketch, "E154.visualSharp", {"position": v(-106.5, 63) * mm});
            skArc(sketch, "E154.filletArc", {"start": v(-104.5, 63) * mm, "mid": v(-105.91, 62.41) * mm, "end": v(-106.5, 61) * mm});
            skPoint(sketch, "E155.visualSharp", {"position": v(-106.5, -63) * mm});
            skArc(sketch, "E155.filletArc", {"start": v(-106.5, -61) * mm, "mid": v(-105.91, -62.41) * mm, "end": v(-104.5, -63) * mm});
            skPoint(sketch, "E156.visualSharp", {"position": v(-61, -108.5) * mm});
            skArc(sketch, "E156.filletArc", {"start": v(-61, -106.5) * mm, "mid": v(-60.41, -107.91) * mm, "end": v(-59, -108.5) * mm});
            skPoint(sketch, "E157.visualSharp", {"position": v(61, -108.5) * mm});
            skArc(sketch, "E157.filletArc", {"start": v(59, -108.5) * mm, "mid": v(60.41, -107.91) * mm, "end": v(61, -106.5) * mm});
            skSolve(sketch);
        }
        {
            var Q0;
            {var subQ4=sQuery(id+"F6.wireOp",EDGE,"E139");Q0=makeQuery(id+"F6.imprint","IMPRINT",FACE,{"disambiguationData":[TD([[makeQuery(id+"F6.imprint","IMPRINT",EDGE,{"derivedFrom":subQ4}),1.0]])]});}
            var Q1;
            Q1=makeQuery(id+"F6.imprint","IMPRINT",FACE,{"disambiguationData":[TD([[makeQuery(id+"F6.imprint","IMPRINT",EDGE,{"derivedFrom":sQuery(id+"F6.wireOp",EDGE,"E143.top")}),-1.0]])]});
            var Q2;
            {var subQ1=sQuery(id+"F6.wireOp",EDGE,"E149.bottom");Q2=makeQuery(id+"F6.imprint","IMPRINT",FACE,{"disambiguationData":[TD([[makeQuery(id+"F6.imprint","IMPRINT",EDGE,{"derivedFrom":subQ1}),-1.0]])]});}
            var Q3;
            {var subQ1=sQuery(id+"F6.wireOp",EDGE,"E145.bottom");Q3=makeQuery(id+"F6.imprint","IMPRINT",FACE,{"disambiguationData":[TD([[makeQuery(id+"F6.imprint","IMPRINT",EDGE,{"derivedFrom":subQ1}),-1.0]])]});}
            var Q4;
            Q4=makeQuery(id+"F6.imprint","IMPRINT",FACE,{"disambiguationData":[TD([[makeQuery(id+"F6.imprint","IMPRINT",EDGE,{"derivedFrom":sQuery(id+"F6.wireOp",EDGE,"E144.top")}),-1.0]])]});
            extrude(context, id + "F7", {"entities" : qUnion([Q0, Q1, Q2, Q3, Q4]), "depth" : 6 * mm, "offsetDistance" : 25 * mm});
        }
        {
            var Q0;
            Q0=qCreatedBy(makeId("Front.planeOp"),FACE);
            var sketch = newSketch(context, id + "F8", { "sketchPlane" : qUnion([Q0])});
            skLineSegment(sketch, "E158.bottom", {"start": v(148, 98) * mm, "end": v(-148, 98) * mm});
            skLineSegment(sketch, "E158.top", {"start": v(148, -98) * mm, "end": v(-148, -98) * mm});
            skLineSegment(sketch, "E158.left", {"start": v(148, 98) * mm, "end": v(148, -98) * mm});
            skLineSegment(sketch, "E158.right", {"start": v(-148, 98) * mm, "end": v(-148, -98) * mm});
            skPoint(sketch, "E158.middle", {"position": v(0, 0) * mm});
            skArc(sketch, "E159", {"start": v(-111, 98) * mm, "mid": v(-121.84, 71.84) * mm, "end": v(-148, 61) * mm});
            skArc(sketch, "E160", {"start": v(111, 98) * mm, "mid": v(121.84, 71.84) * mm, "end": v(148, 61) * mm});
            skArc(sketch, "E161", {"start": v(148, -61) * mm, "mid": v(121.84, -71.84) * mm, "end": v(111, -98) * mm});
            skArc(sketch, "E162", {"start": v(-148, -61) * mm, "mid": v(-121.84, -71.84) * mm, "end": v(-111, -98) * mm});
            skLineSegment(sketch, "E163.bottom", {"start": v(-111, 98) * mm, "end": v(111, 98) * mm});
            skLineSegment(sketch, "E164.bottom", {"start": v(-111, -98) * mm, "end": v(111, -98) * mm});
            skLineSegment(sketch, "E165.bottom", {"start": v(-148, -61) * mm, "end": v(-154.5, -61) * mm});
            skLineSegment(sketch, "E165.top", {"start": v(-148, 61) * mm, "end": v(-154.5, 61) * mm});
            skLineSegment(sketch, "E165.left", {"start": v(-148, -61) * mm, "end": v(-148, 61) * mm});
            skLineSegment(sketch, "E165.right", {"start": v(-156.5, -59) * mm, "end": v(-156.5, 59) * mm});
            skLineSegment(sketch, "E166.bottom", {"start": v(148, 61) * mm, "end": v(154.5, 61) * mm});
            skLineSegment(sketch, "E166.top", {"start": v(148, -61) * mm, "end": v(154.5, -61) * mm});
            skLineSegment(sketch, "E166.left", {"start": v(148, 61) * mm, "end": v(148, -61) * mm});
            skLineSegment(sketch, "E166.right", {"start": v(156.5, 59) * mm, "end": v(156.5, -59) * mm});
            skPoint(sketch, "E167.visualSharp", {"position": v(-156.5, 61) * mm});
            skArc(sketch, "E167.filletArc", {"start": v(-154.5, 61) * mm, "mid": v(-155.91, 60.41) * mm, "end": v(-156.5, 59) * mm});
            skPoint(sketch, "E168.visualSharp", {"position": v(-156.5, -61) * mm});
            skArc(sketch, "E168.filletArc", {"start": v(-156.5, -59) * mm, "mid": v(-155.91, -60.41) * mm, "end": v(-154.5, -61) * mm});
            skPoint(sketch, "E169.visualSharp", {"position": v(156.5, 61) * mm});
            skArc(sketch, "E169.filletArc", {"start": v(156.5, 59) * mm, "mid": v(155.91, 60.41) * mm, "end": v(154.5, 61) * mm});
            skPoint(sketch, "E170.visualSharp", {"position": v(156.5, -61) * mm});
            skArc(sketch, "E170.filletArc", {"start": v(154.5, -61) * mm, "mid": v(155.91, -60.41) * mm, "end": v(156.5, -59) * mm});
            skSolve(sketch);
        }
        {
            var Q0;
            {var subQ0=sQuery(id+"F8.wireOp",EDGE,"E159");Q0=makeQuery(id+"F8.imprint","IMPRINT",FACE,{"disambiguationData":[TD([[makeQuery(id+"F8.imprint","IMPRINT",EDGE,{"derivedFrom":subQ0}),1.0]])]});}
            var Q1;
            Q1=makeQuery(id+"F8.imprint","IMPRINT",FACE,{"disambiguationData":[TD([[makeQuery(id+"F8.imprint","IMPRINT",EDGE,{"derivedFrom":sQuery(id+"F8.wireOp",EDGE,"E163.bottom")}),1.0]])]});
            var Q2;
            {var subQ1=sQuery(id+"F8.wireOp",EDGE,"E166.bottom");Q2=makeQuery(id+"F8.imprint","IMPRINT",FACE,{"disambiguationData":[TD([[makeQuery(id+"F8.imprint","IMPRINT",EDGE,{"derivedFrom":subQ1}),-1.0]])]});}
            var Q3;
            Q3=makeQuery(id+"F8.imprint","IMPRINT",FACE,{"disambiguationData":[TD([[makeQuery(id+"F8.imprint","IMPRINT",EDGE,{"derivedFrom":sQuery(id+"F8.wireOp",EDGE,"E164.bottom")}),-1.0]])]});
            var Q4;
            {var subQ1=sQuery(id+"F8.wireOp",EDGE,"E165.bottom");Q4=makeQuery(id+"F8.imprint","IMPRINT",FACE,{"disambiguationData":[TD([[makeQuery(id+"F8.imprint","IMPRINT",EDGE,{"derivedFrom":subQ1}),-1.0]])]});}
            extrude(context, id + "F9", {"entities" : qUnion([Q0, Q1, Q2, Q3, Q4]), "depth" : 6 * mm, "offsetDistance" : 25 * mm});
        }
        {
            var Q0;
            Q0=qCreatedBy(makeId("Front.planeOp"),FACE);
            var sketch = newSketch(context, id + "F10", { "sketchPlane" : qUnion([Q0])});
            skLineSegment(sketch, "E171.bottom", {"start": v(148, 98) * mm, "end": v(-148, 98) * mm});
            skLineSegment(sketch, "E171.top", {"start": v(148, -98) * mm, "end": v(-148, -98) * mm});
            skLineSegment(sketch, "E171.left", {"start": v(148, 98) * mm, "end": v(148, -98) * mm});
            skLineSegment(sketch, "E171.right", {"start": v(-148, 98) * mm, "end": v(-148, -98) * mm});
            skPoint(sketch, "E171.middle", {"position": v(0, 0) * mm});
            skArc(sketch, "E172", {"start": v(-111, 98) * mm, "mid": v(-121.84, 71.84) * mm, "end": v(-148, 61) * mm});
            skArc(sketch, "E173", {"start": v(111, 98) * mm, "mid": v(121.84, 71.84) * mm, "end": v(148, 61) * mm});
            skArc(sketch, "E174", {"start": v(148, -61) * mm, "mid": v(121.84, -71.84) * mm, "end": v(111, -98) * mm});
            skArc(sketch, "E175", {"start": v(-148, -61) * mm, "mid": v(-121.84, -71.84) * mm, "end": v(-111, -98) * mm});
            skLineSegment(sketch, "E176.bottom", {"start": v(-111, 98) * mm, "end": v(111, 98) * mm});
            skLineSegment(sketch, "E176.top", {"start": v(-109, 106.5) * mm, "end": v(109, 106.5) * mm});
            skLineSegment(sketch, "E176.left", {"start": v(-111, 98) * mm, "end": v(-111, 104.5) * mm});
            skLineSegment(sketch, "E176.right", {"start": v(111, 98) * mm, "end": v(111, 104.5) * mm});
            skLineSegment(sketch, "E177.bottom", {"start": v(-111, -98) * mm, "end": v(111, -98) * mm});
            skLineSegment(sketch, "E177.top", {"start": v(-109, -106.5) * mm, "end": v(109, -106.5) * mm});
            skLineSegment(sketch, "E177.left", {"start": v(-111, -98) * mm, "end": v(-111, -104.5) * mm});
            skLineSegment(sketch, "E177.right", {"start": v(111, -98) * mm, "end": v(111, -104.5) * mm});
            skLineSegment(sketch, "E178.bottom", {"start": v(-148, -61) * mm, "end": v(-154.5, -61) * mm});
            skLineSegment(sketch, "E178.top", {"start": v(-148, 61) * mm, "end": v(-154.5, 61) * mm});
            skLineSegment(sketch, "E178.left", {"start": v(-148, -61) * mm, "end": v(-148, 61) * mm});
            skLineSegment(sketch, "E178.right", {"start": v(-156.5, -59) * mm, "end": v(-156.5, 59) * mm});
            skLineSegment(sketch, "E179.bottom", {"start": v(148, -61) * mm, "end": v(154.5, -61) * mm});
            skLineSegment(sketch, "E179.top", {"start": v(148, 61) * mm, "end": v(154.5, 61) * mm});
            skLineSegment(sketch, "E179.left", {"start": v(148, -61) * mm, "end": v(148, 61) * mm});
            skLineSegment(sketch, "E179.right", {"start": v(156.5, -59) * mm, "end": v(156.5, 59) * mm});
            skLineSegment(sketch, "E180.bottom", {"start": v(22.5, 22.5) * mm, "end": v(-22.5, 22.5) * mm});
            skLineSegment(sketch, "E180.top", {"start": v(22.5, -22.5) * mm, "end": v(-22.5, -22.5) * mm});
            skLineSegment(sketch, "E180.left", {"start": v(22.5, 22.5) * mm, "end": v(22.5, -22.5) * mm});
            skLineSegment(sketch, "E180.right", {"start": v(-22.5, 22.5) * mm, "end": v(-22.5, -22.5) * mm});
            skCircle(sketch, "E181", {"center": v(0, 0) * mm, "radius": 14.5 * mm});
            skPoint(sketch, "E182", {"position": v(-14.5, 14.5) * mm});
            skCircle(sketch, "E183", {"center": v(-14.5, 14.5) * mm, "radius": 2.25 * mm});
            skCircle(sketch, "E184.0.1.0", {"center": v(-14.5, -14.5) * mm, "radius": 2.25 * mm});
            skPoint(sketch, "E184.0.1.1", {"position": v(-14.5, -14.5) * mm});
            skCircle(sketch, "E184.1.0.0", {"center": v(14.5, 14.5) * mm, "radius": 2.25 * mm});
            skPoint(sketch, "E184.1.0.1", {"position": v(14.5, 14.5) * mm});
            skCircle(sketch, "E184.1.1.0", {"center": v(14.5, -14.5) * mm, "radius": 2.25 * mm});
            skPoint(sketch, "E184.1.1.1", {"position": v(14.5, -14.5) * mm});
            skLineSegment(sketch, "E184.direction1", {"start": v(-14.5, 14.5) * mm, "end": v(14.5, 14.5) * mm, "construction": true});
            skLineSegment(sketch, "E184.direction2", {"start": v(-14.5, 14.5) * mm, "end": v(-14.5, -14.5) * mm, "construction": true});
            skPoint(sketch, "E185.visualSharp", {"position": v(-111, 106.5) * mm});
            skArc(sketch, "E185.filletArc", {"start": v(-109, 106.5) * mm, "mid": v(-110.41, 105.91) * mm, "end": v(-111, 104.5) * mm});
            skPoint(sketch, "E186.visualSharp", {"position": v(-156.5, 61) * mm});
            skArc(sketch, "E186.filletArc", {"start": v(-154.5, 61) * mm, "mid": v(-155.91, 60.41) * mm, "end": v(-156.5, 59) * mm});
            skPoint(sketch, "E187.visualSharp", {"position": v(111, 106.5) * mm});
            skArc(sketch, "E187.filletArc", {"start": v(111, 104.5) * mm, "mid": v(110.41, 105.91) * mm, "end": v(109, 106.5) * mm});
            skPoint(sketch, "E188.visualSharp", {"position": v(156.5, 61) * mm});
            skArc(sketch, "E188.filletArc", {"start": v(156.5, 59) * mm, "mid": v(155.91, 60.41) * mm, "end": v(154.5, 61) * mm});
            skPoint(sketch, "E189.visualSharp", {"position": v(156.5, -61) * mm});
            skArc(sketch, "E189.filletArc", {"start": v(154.5, -61) * mm, "mid": v(155.91, -60.41) * mm, "end": v(156.5, -59) * mm});
            skPoint(sketch, "E190.visualSharp", {"position": v(-156.5, -61) * mm});
            skArc(sketch, "E190.filletArc", {"start": v(-156.5, -59) * mm, "mid": v(-155.91, -60.41) * mm, "end": v(-154.5, -61) * mm});
            skPoint(sketch, "E191.visualSharp", {"position": v(-111, -106.5) * mm});
            skArc(sketch, "E191.filletArc", {"start": v(-111, -104.5) * mm, "mid": v(-110.41, -105.91) * mm, "end": v(-109, -106.5) * mm});
            skPoint(sketch, "E192.visualSharp", {"position": v(111, -106.5) * mm});
            skArc(sketch, "E192.filletArc", {"start": v(109, -106.5) * mm, "mid": v(110.41, -105.91) * mm, "end": v(111, -104.5) * mm});
            skSolve(sketch);
        }
        {
            var Q0;
            {var subQ4=sQuery(id+"F10.wireOp",EDGE,"E172");Q0=makeQuery(id+"F10.imprint","IMPRINT",FACE,{"disambiguationData":[TD([[makeQuery(id+"F10.imprint","IMPRINT",EDGE,{"derivedFrom":subQ4}),1.0]])]});}
            var Q1;
            Q1=makeQuery(id+"F10.imprint","IMPRINT",FACE,{"disambiguationData":[TD([[makeQuery(id+"F10.imprint","IMPRINT",EDGE,{"derivedFrom":sQuery(id+"F10.wireOp",EDGE,"E180.bottom")}),1.0]])]});
            var Q2;
            Q2=makeQuery(id+"F10.imprint","IMPRINT",FACE,{"disambiguationData":[TD([[makeQuery(id+"F10.imprint","IMPRINT",EDGE,{"derivedFrom":sQuery(id+"F10.wireOp",EDGE,"E176.top")}),-1.0]])]});
            var Q3;
            {var subQ0=sQuery(id+"F10.wireOp",EDGE,"E179.bottom");Q3=makeQuery(id+"F10.imprint","IMPRINT",FACE,{"disambiguationData":[TD([[makeQuery(id+"F10.imprint","IMPRINT",EDGE,{"derivedFrom":subQ0}),1.0]])]});}
            var Q4;
            {var subQ1=sQuery(id+"F10.wireOp",EDGE,"E178.bottom");Q4=makeQuery(id+"F10.imprint","IMPRINT",FACE,{"disambiguationData":[TD([[makeQuery(id+"F10.imprint","IMPRINT",EDGE,{"derivedFrom":subQ1}),-1.0]])]});}
            var Q5;
            Q5=makeQuery(id+"F10.imprint","IMPRINT",FACE,{"disambiguationData":[TD([[makeQuery(id+"F10.imprint","IMPRINT",EDGE,{"derivedFrom":sQuery(id+"F10.wireOp",EDGE,"E177.top")}),1.0]])]});
            extrude(context, id + "F11", {"entities" : qUnion([Q0, Q1, Q2, Q3, Q4, Q5]), "depth" : 6 * mm, "offsetDistance" : 25 * mm});
        }
        {
            var Q0;
            Q0=qCreatedBy(makeId("Front.planeOp"),FACE);
            var sketch = newSketch(context, id + "F12", { "sketchPlane" : qUnion([Q0])});
            skLineSegment(sketch, "E193.bottom", {"start": v(176, 130) * mm, "end": v(-176, 130) * mm});
            skLineSegment(sketch, "E193.top", {"start": v(178, -130) * mm, "end": v(-178, -130) * mm});
            skLineSegment(sketch, "E193.left", {"start": v(178, 128) * mm, "end": v(178, -130) * mm});
            skLineSegment(sketch, "E193.right", {"start": v(-178, 128) * mm, "end": v(-178, -130) * mm});
            skPoint(sketch, "E193.middle", {"position": v(0, 0) * mm});
            skLineSegment(sketch, "E194.bottom", {"start": v(-178, -130) * mm, "end": v(-148, -130) * mm});
            skLineSegment(sketch, "E194.top", {"start": v(-176, -160) * mm, "end": v(-148, -160) * mm});
            skLineSegment(sketch, "E194.left", {"start": v(-178, -130) * mm, "end": v(-178, -158) * mm});
            skLineSegment(sketch, "E194.right", {"start": v(-148, -130) * mm, "end": v(-148, -160) * mm});
            skLineSegment(sketch, "E195.bottom", {"start": v(178, -130) * mm, "end": v(148, -130) * mm});
            skLineSegment(sketch, "E195.top", {"start": v(176, -160) * mm, "end": v(148, -160) * mm});
            skLineSegment(sketch, "E195.left", {"start": v(178, -130) * mm, "end": v(178, -158) * mm});
            skLineSegment(sketch, "E195.right", {"start": v(148, -130) * mm, "end": v(148, -160) * mm});
            skArc(sketch, "E196", {"start": v(148, -160) * mm, "mid": v(0, -132.88) * mm, "end": v(-148, -160) * mm});
            skLineSegment(sketch, "E197.bottom", {"start": v(148, 98) * mm, "end": v(-148, 98) * mm});
            skLineSegment(sketch, "E197.top", {"start": v(148, -98) * mm, "end": v(-148, -98) * mm});
            skLineSegment(sketch, "E197.left", {"start": v(148, 98) * mm, "end": v(148, -98) * mm});
            skLineSegment(sketch, "E197.right", {"start": v(-148, 98) * mm, "end": v(-148, -98) * mm});
            skPoint(sketch, "E198", {"position": v(-163, 80) * mm});
            skCircle(sketch, "E199", {"center": v(-163, 80) * mm, "radius": 3.5 * mm});
            skPoint(sketch, "E200", {"position": v(163, 80) * mm});
            skPoint(sketch, "E201", {"position": v(-163, -70) * mm});
            skPoint(sketch, "E202", {"position": v(163, -70) * mm});
            skCircle(sketch, "E203", {"center": v(163, 80) * mm, "radius": 3.5 * mm});
            skCircle(sketch, "E204", {"center": v(-163, -70) * mm, "radius": 3.5 * mm});
            skCircle(sketch, "E205", {"center": v(163, -70) * mm, "radius": 3.5 * mm});
            skPoint(sketch, "E206.visualSharp", {"position": v(-178, 130) * mm});
            skArc(sketch, "E206.filletArc", {"start": v(-176, 130) * mm, "mid": v(-177.41, 129.41) * mm, "end": v(-178, 128) * mm});
            skPoint(sketch, "E207.visualSharp", {"position": v(-178, -160) * mm});
            skArc(sketch, "E207.filletArc", {"start": v(-178, -158) * mm, "mid": v(-177.41, -159.41) * mm, "end": v(-176, -160) * mm});
            skPoint(sketch, "E208.visualSharp", {"position": v(178, -160) * mm});
            skArc(sketch, "E208.filletArc", {"start": v(176, -160) * mm, "mid": v(177.41, -159.41) * mm, "end": v(178, -158) * mm});
            skPoint(sketch, "E209.visualSharp", {"position": v(178, 130) * mm});
            skArc(sketch, "E209.filletArc", {"start": v(178, 128) * mm, "mid": v(177.41, 129.41) * mm, "end": v(176, 130) * mm});
            skSolve(sketch);
        }
        {
            var Q0;
            Q0=makeQuery(id+"F12.imprint","IMPRINT",FACE,{"disambiguationData":[TD([[makeQuery(id+"F12.imprint","IMPRINT",EDGE,{"derivedFrom":sQuery(id+"F12.wireOp",EDGE,"E193.bottom")}),1.0]])]});
            var Q1;
            {var subQ2=sQuery(id+"F12.wireOp",EDGE,"E194.right");Q1=makeQuery(id+"F12.imprint","IMPRINT",FACE,{"disambiguationData":[TD([[makeQuery(id+"F12.imprint","IMPRINT",EDGE,{"derivedFrom":subQ2}),1.0]])]});}
            var Q2;
            Q2=makeQuery(id+"F12.imprint","IMPRINT",FACE,{"disambiguationData":[TD([[makeQuery(id+"F12.imprint","IMPRINT",EDGE,{"derivedFrom":sQuery(id+"F12.wireOp",EDGE,"E194.top")}),1.0]])]});
            var Q3;
            Q3=makeQuery(id+"F12.imprint","IMPRINT",FACE,{"disambiguationData":[TD([[makeQuery(id+"F12.imprint","IMPRINT",EDGE,{"derivedFrom":sQuery(id+"F12.wireOp",EDGE,"E195.top")}),-1.0]])]});
            var Q4;
            Q4=makeQuery(id+"F12.imprint","IMPRINT",FACE,{"disambiguationData":[TD([[makeQuery(id+"F12.imprint","IMPRINT",EDGE,{"derivedFrom":sQuery(id+"F12.wireOp",EDGE,"E197.bottom")}),1.0]])]});
            extrude(context, id + "F13", {"entities" : qUnion([Q0, Q1, Q2, Q3, Q4]), "depth" : 6 * mm, "offsetDistance" : 25 * mm});
        }
    });
